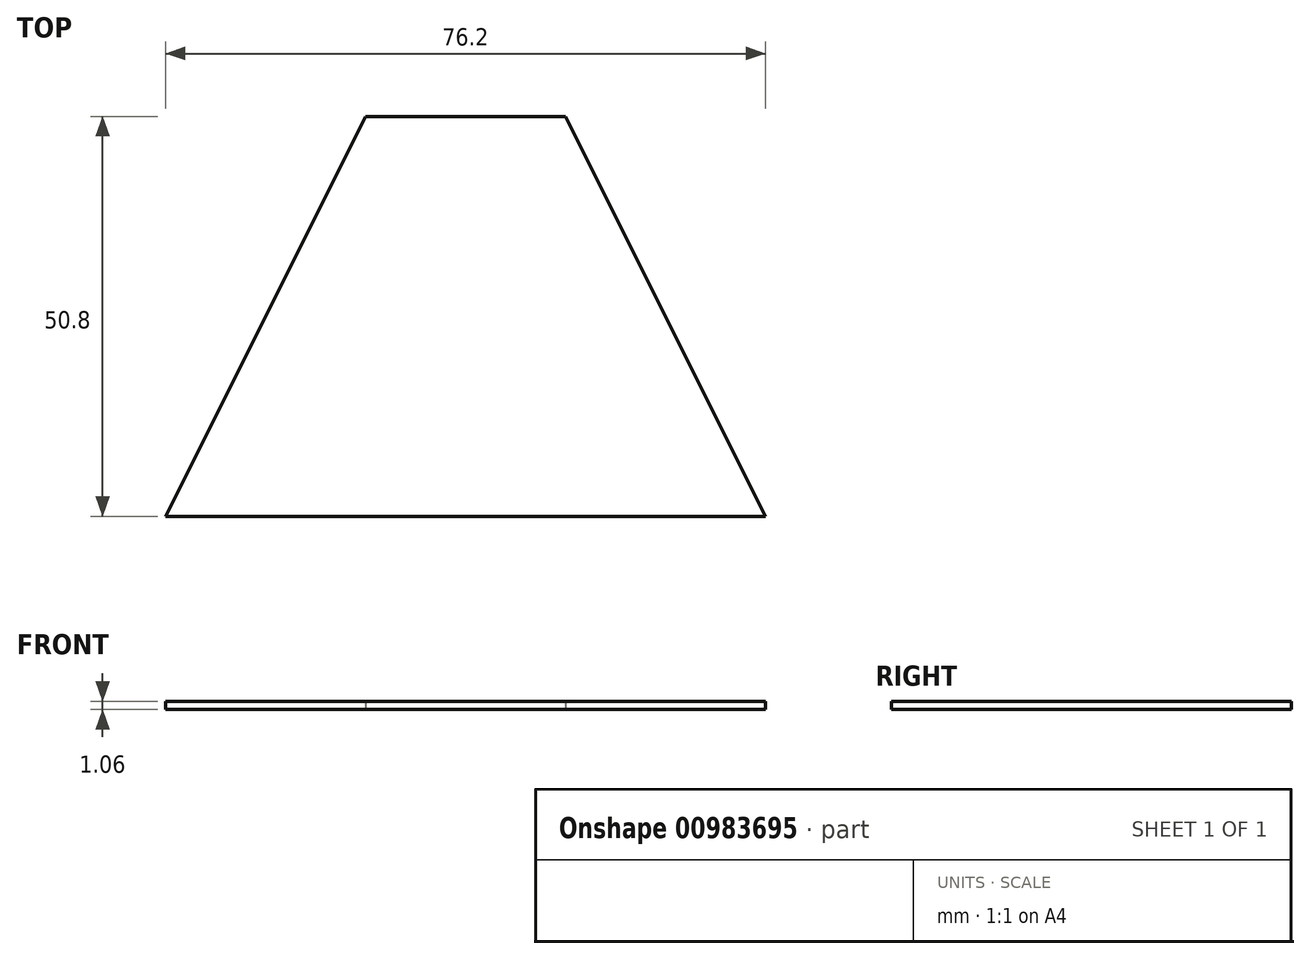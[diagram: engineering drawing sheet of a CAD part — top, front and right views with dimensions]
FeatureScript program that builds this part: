
annotation { "Feature Type Name" : "Feature", "Feature Type Description" : "" }
export const myFeature = defineFeature(function(context is Context, id is Id, definition is map)
    precondition{}
    {
        {
            var Q0;
            Q0=qCreatedBy(makeId("Top.planeOp"),FACE);
            var sketch = newSketch(context, id + "F0", { "sketchPlane" : qUnion([Q0])});
            skLineSegment(sketch, "E0.bottom", {"start": v(12.7, -25.4) * mm, "end": v(-12.7, -25.4) * mm});
            skLineSegment(sketch, "E0.top", {"start": v(12.7, 25.4) * mm, "end": v(-12.7, 25.4) * mm});
            skPoint(sketch, "E0.middle", {"position": v(0, 0) * mm});
            skLineSegment(sketch, "E1", {"start": v(-12.7, 25.4) * mm, "end": v(-38.1, -25.4) * mm});
            skLineSegment(sketch, "E2", {"start": v(-38.1, -25.4) * mm, "end": v(-12.7, -25.4) * mm});
            skLineSegment(sketch, "E3", {"start": v(12.7, -25.4) * mm, "end": v(38.1, -25.4) * mm});
            skLineSegment(sketch, "E4", {"start": v(38.1, -25.4) * mm, "end": v(12.7, 25.4) * mm});
            skSolve(sketch);
        }
        {
            var Q0;
            Q0 = qSketchRegion(id + "F0", true);
            extrude(context, id + "F1", {"entities" : qUnion([Q0]), "depth" : 1.06 * mm, "offsetDistance" : 25.4 * mm});
        }
    });
